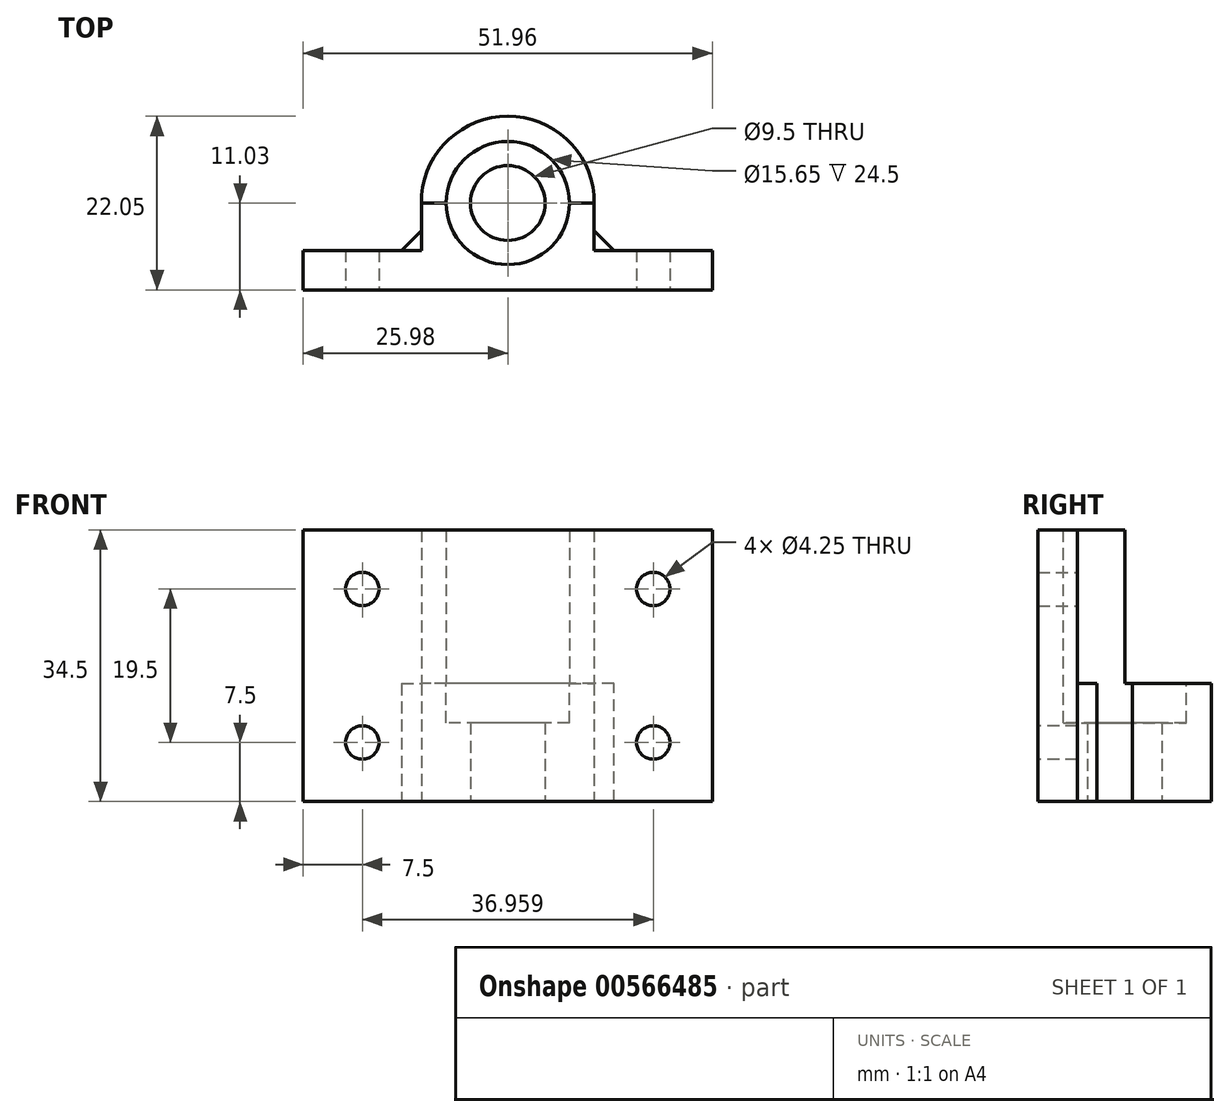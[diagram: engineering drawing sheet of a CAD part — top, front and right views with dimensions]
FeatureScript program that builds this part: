
annotation { "Feature Type Name" : "Feature", "Feature Type Description" : "" }
export const myFeature = defineFeature(function(context is Context, id is Id, definition is map)
    precondition{}
    {
        {
            var Q0;
            Q0=qCreatedBy(makeId("Top.planeOp"),FACE);
            var sketch = newSketch(context, id + "F0", { "sketchPlane" : qUnion([Q0])});
            skCircle(sketch, "E0", {"center": v(0, 0) * mm, "radius": 4.75 * mm});
            skCircle(sketch, "E1", {"center": v(0, 0) * mm, "radius": 7.83 * mm, "construction": true});
            skLineSegment(sketch, "E2", {"start": v(0, -11.03) * mm, "end": v(25.98, -11.03) * mm});
            skLineSegment(sketch, "E3", {"start": v(25.98, -11.03) * mm, "end": v(25.98, -6.02) * mm});
            skLineSegment(sketch, "E4", {"start": v(25.98, -6.02) * mm, "end": v(10.98, -6.03) * mm});
            skLineSegment(sketch, "E5", {"start": v(10.98, -6.03) * mm, "end": v(10.98, 1) * mm});
            skArc(sketch, "E6", {"start": v(10.98, 1) * mm, "mid": v(7.43, 8.14) * mm, "end": v(0, 11.03) * mm});
            skArc(sketch, "E7.MirrorCS", {"start": v(-10.98, 1) * mm, "mid": v(-7.43, 8.14) * mm, "end": v(0, 11.03) * mm});
            skLineSegment(sketch, "E8.MirrorCS", {"start": v(-10.98, -6.03) * mm, "end": v(-10.98, 1) * mm});
            skLineSegment(sketch, "E9.MirrorCS", {"start": v(-25.98, -6.02) * mm, "end": v(-10.98, -6.03) * mm});
            skLineSegment(sketch, "E10.MirrorCS", {"start": v(-25.98, -11.03) * mm, "end": v(-25.98, -6.02) * mm});
            skLineSegment(sketch, "E11.MirrorCS", {"start": v(0, -11.03) * mm, "end": v(-25.98, -11.03) * mm});
            skSolve(sketch);
        }
        {
            var Q0;
            Q0=qSketchRegion(id+"F0",true);
            extrude(context, id + "F1", {"entities" : qUnion([Q0]), "endBound" : BoundingType.SYMMETRIC, "depth" : 15 * mm});
        }
        {
            var Q0;
            Q0=makeQuery(id+"F1.opExtrude","SWEPT_FACE",FACE,{"disambiguationData":[OSD([sQuery(id+"F0.wireOp",EDGE,"E2"),sQuery(id+"F0.wireOp",EDGE,"E11.MirrorCS")])]});
            var sketch = newSketch(context, id + "F2", { "sketchPlane" : qUnion([Q0])});
            skCircle(sketch, "E12", {"center": v(-18.48, 0) * mm, "radius": 2.12 * mm});
            skCircle(sketch, "E13.MirrorC", {"center": v(18.48, 0) * mm, "radius": 2.12 * mm});
            skSolve(sketch);
        }
        {
            var Q0;
            Q0=qSketchRegion(id+"F2",true);
            extrude(context, id + "F3", {"entities" : qUnion([Q0]), "operationType" : NewBodyOperationType.REMOVE, "oppositeDirection" : true, "depth" : 25 * mm});
        }
        {
            var Q0;
            Q0=makeQuery(id+"F1.opExtrude","CAP_FACE",FACE,{"disambiguationData":[OSD([sQuery(id+"F0.wireOp",EDGE,"E0"),sQuery(id+"F0.wireOp",EDGE,"E2"),sQuery(id+"F0.wireOp",EDGE,"E3"),sQuery(id+"F0.wireOp",EDGE,"E4"),sQuery(id+"F0.wireOp",EDGE,"E5"),sQuery(id+"F0.wireOp",EDGE,"E6"),sQuery(id+"F0.wireOp",EDGE,"E7.MirrorCS"),sQuery(id+"F0.wireOp",EDGE,"E8.MirrorCS"),sQuery(id+"F0.wireOp",EDGE,"E9.MirrorCS"),sQuery(id+"F0.wireOp",EDGE,"E10.MirrorCS"),sQuery(id+"F0.wireOp",EDGE,"E11.MirrorCS")])],"isStart":false});
            var sketch = newSketch(context, id + "F4", { "sketchPlane" : qUnion([Q0])});
            skCircle(sketch, "E14", {"center": v(0, 0) * mm, "radius": 7.83 * mm});
            skSolve(sketch);
        }
        {
            var Q0;
            Q0=qSketchRegion(id+"F4",true);
            extrude(context, id + "F5", {"entities" : qUnion([Q0]), "operationType" : NewBodyOperationType.REMOVE, "oppositeDirection" : true, "depth" : 5 * mm});
        }
        {
            var Q0;
            Q0=makeQuery(id+"F1.opExtrude","SWEPT_EDGE",EDGE,{"disambiguationData":[OSD([sQuery(id+"F0.wireOp",EDGE,"E8.MirrorCS"),sQuery(id+"F0.wireOp",EDGE,"E9.MirrorCS")])]});
            var Q1;
            Q1=makeQuery(id+"F1.opExtrude","SWEPT_EDGE",EDGE,{"disambiguationData":[OSD([sQuery(id+"F0.wireOp",EDGE,"E4"),sQuery(id+"F0.wireOp",EDGE,"E5")])]});
            chamfer(context, id + "F6", {"entities" : qUnion([Q0, Q1]), "width" : 2.5 * mm, "tangentPropagation" : true});
        }
        {
            var Q0;
            Q0=makeQuery(id+"F1.opExtrude","CAP_FACE",FACE,{"disambiguationData":[OSD([sQuery(id+"F0.wireOp",EDGE,"E0"),sQuery(id+"F0.wireOp",EDGE,"E2"),sQuery(id+"F0.wireOp",EDGE,"E3"),sQuery(id+"F0.wireOp",EDGE,"E4"),sQuery(id+"F0.wireOp",EDGE,"E5"),sQuery(id+"F0.wireOp",EDGE,"E6"),sQuery(id+"F0.wireOp",EDGE,"E7.MirrorCS"),sQuery(id+"F0.wireOp",EDGE,"E8.MirrorCS"),sQuery(id+"F0.wireOp",EDGE,"E9.MirrorCS"),sQuery(id+"F0.wireOp",EDGE,"E10.MirrorCS"),sQuery(id+"F0.wireOp",EDGE,"E11.MirrorCS")])],"isStart":false});
            var sketch = newSketch(context, id + "F7", { "sketchPlane" : qUnion([Q0])});
            skLineSegment(sketch, "E15", {"start": v(0, -11.03) * mm, "end": v(25.98, -11.03) * mm});
            skLineSegment(sketch, "E16", {"start": v(25.98, -11.03) * mm, "end": v(25.98, -6.02) * mm});
            skLineSegment(sketch, "E17", {"start": v(25.98, -6.02) * mm, "end": v(10.98, -6.03) * mm});
            skLineSegment(sketch, "E18", {"start": v(10.98, -6.03) * mm, "end": v(10.98, 0) * mm});
            skArc(sketch, "E19", {"start": v(7.83, 0) * mm, "mid": v(0, -7.83) * mm, "end": v(-7.83, 0) * mm});
            skLineSegment(sketch, "E20", {"start": v(7.83, 0) * mm, "end": v(10.98, 0) * mm});
            skLineSegment(sketch, "E21.MirrorCS", {"start": v(-7.83, 0) * mm, "end": v(-10.98, 0) * mm});
            skLineSegment(sketch, "E22.MirrorCS", {"start": v(-10.98, -6.03) * mm, "end": v(-10.98, 0) * mm});
            skLineSegment(sketch, "E23.MirrorCS", {"start": v(-25.98, -6.02) * mm, "end": v(-10.98, -6.03) * mm});
            skLineSegment(sketch, "E24.MirrorCS", {"start": v(-25.98, -11.03) * mm, "end": v(-25.98, -6.02) * mm});
            skLineSegment(sketch, "E25.MirrorCS", {"start": v(0, -11.03) * mm, "end": v(-25.98, -11.03) * mm});
            skSolve(sketch);
        }
        {
            var Q0;
            Q0=qSketchRegion(id+"F7",true);
            extrude(context, id + "F8", {"entities" : qUnion([Q0]), "operationType" : NewBodyOperationType.ADD, "depth" : 19.5 * mm});
        }
        {
            var Q0;
            Q0=makeQuery(id+"F8.boolean.opBoolean","MERGE",FACE,{"derivedFrom":[makeQuery(id+"F1.opExtrude","SWEPT_FACE",FACE,{"disambiguationData":[OSD([sQuery(id+"F0.wireOp",EDGE,"E9.MirrorCS")])]}),makeQuery(id+"F8.opExtrude","SWEPT_FACE",FACE,{"disambiguationData":[OSD([sQuery(id+"F7.wireOp",EDGE,"E23.MirrorCS")])]})]});
            var sketch = newSketch(context, id + "F9", { "sketchPlane" : qUnion([Q0])});
            skCircle(sketch, "E26", {"center": v(-18.48, 19.5) * mm, "radius": 2.12 * mm});
            skCircle(sketch, "E27.MirrorC", {"center": v(18.48, 19.5) * mm, "radius": 2.12 * mm});
            skSolve(sketch);
        }
        {
            var Q0;
            Q0=qSketchRegion(id+"F9",true);
            extrude(context, id + "F10", {"entities" : qUnion([Q0]), "operationType" : NewBodyOperationType.REMOVE, "oppositeDirection" : true, "depth" : 25 * mm});
        }
    });
